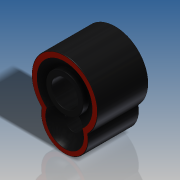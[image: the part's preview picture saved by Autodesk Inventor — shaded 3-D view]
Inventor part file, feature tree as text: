
AUTODESK INVENTOR PART (.ipt)
format: ipt  version: 2016 SP2 (Build 200236200, 236)  size: 288,256 bytes
history: native  units: in
note: dims shown in document units (in); Inventor stores cm internally (conversion verified against a paired STEP export)
features: sketch x2, extrude x2, revolve x2, fillet x1
ambient origin geometry x8: Origin, YZ Plane, XZ Plane, XY Plane, X Axis, Y Axis, Z Axis, Center Point
bodies: Solid1 (feature_tree)
feature tree (7):
  sketch  "Sketch2"  dims[d0=0.4724in d1=0.3386in]
  extrude  "Extrusion1"  Depth=0.3386in
  sketch  "Sketch3"  dims[d2=0.2047in d3=0.3622in d4=0.0in d5=0.126in d6=0.2677in d7=0.189in d8=0.3937in d9=0.2709in d10=0.3465in d11=0.2147in d12=0.0394in d13=0.2869in d14=90.0deg d15=0.1575in d16=0.063in d17=90.0deg d18=0.3622in d19=0.0in d20=0.0039in]
  revolve  "Revolution1"  [1 undecoded]
  revolve  "Revolution2"  [1 undecoded]
  extrude  "Extrusion2"  Depth=0.0039in
  fillet  "Fillet1"  Radius=0.189in
note: 2 required parameter values undecoded (feature->parameter linkage not recoverable at this tier; creation-order binding heuristic only, values carry confidence <= 0.55)
